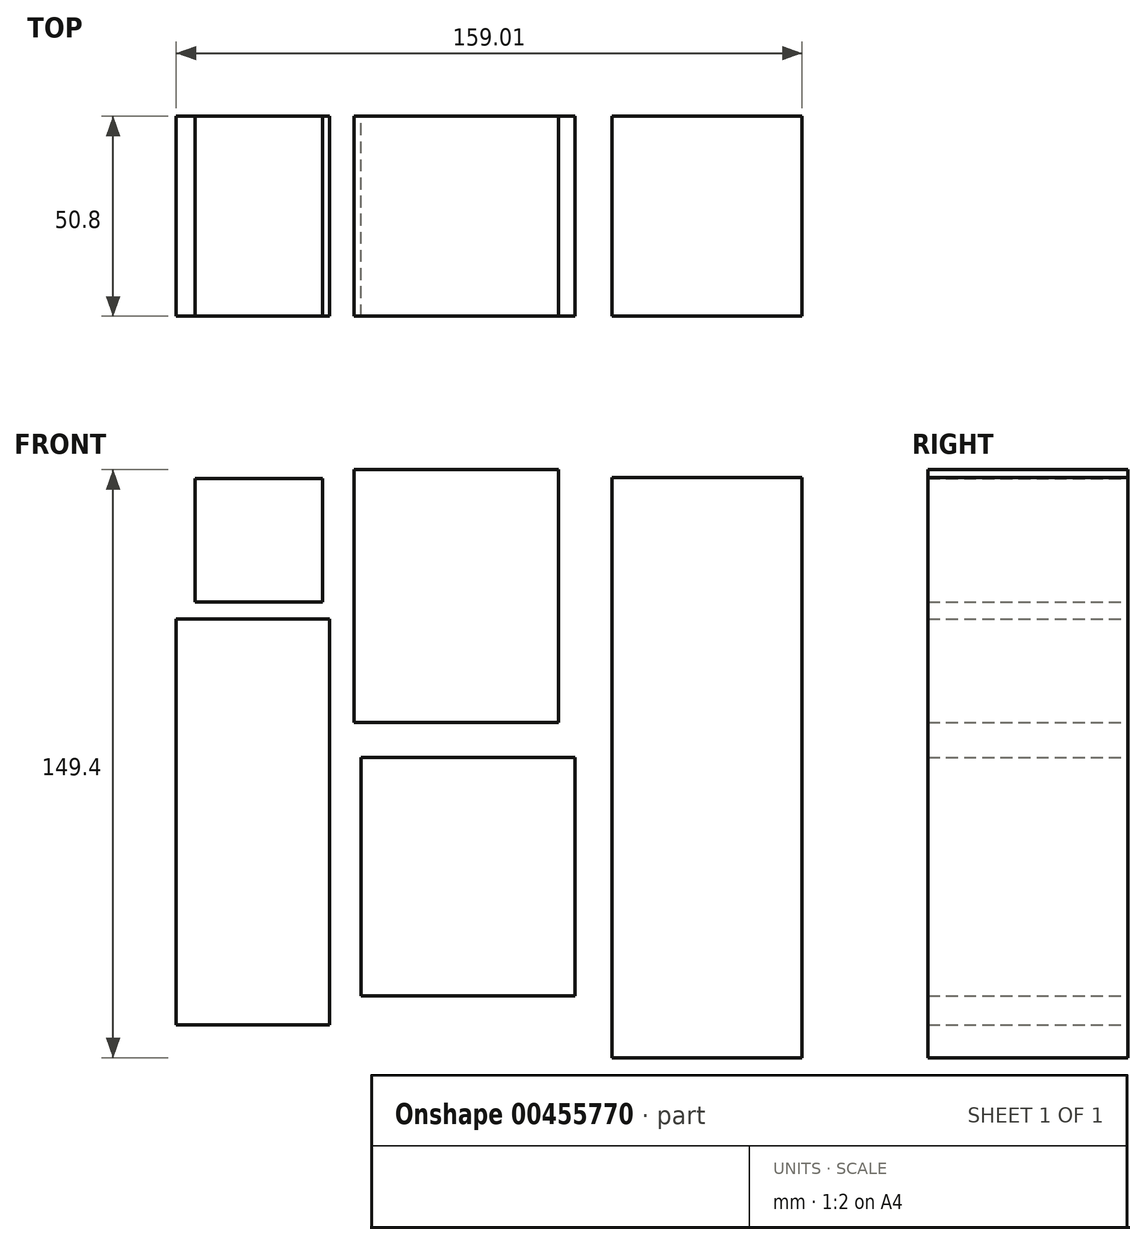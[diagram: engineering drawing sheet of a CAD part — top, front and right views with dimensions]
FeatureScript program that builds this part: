
annotation { "Feature Type Name" : "Feature", "Feature Type Description" : "" }
export const myFeature = defineFeature(function(context is Context, id is Id, definition is map)
    precondition{}
    {
        {
            var Q0;
            Q0=qCreatedBy(makeId("Front.planeOp"),FACE);
            var sketch = newSketch(context, id + "F0", { "sketchPlane" : qUnion([Q0])});
            skLineSegment(sketch, "E0.bottom", {"start": v(-22.75, 73.18) * mm, "end": v(29.07, 73.18) * mm});
            skLineSegment(sketch, "E0.top", {"start": v(-22.75, 8.97) * mm, "end": v(29.07, 8.97) * mm});
            skLineSegment(sketch, "E0.left", {"start": v(-22.75, 73.18) * mm, "end": v(-22.75, 8.97) * mm});
            skLineSegment(sketch, "E0.right", {"start": v(29.07, 73.18) * mm, "end": v(29.07, 8.97) * mm});
            skLineSegment(sketch, "E1.bottom", {"start": v(-29.07, 35.27) * mm, "end": v(-68, 35.27) * mm});
            skLineSegment(sketch, "E1.top", {"start": v(-29.07, -67.88) * mm, "end": v(-68, -67.88) * mm});
            skLineSegment(sketch, "E1.left", {"start": v(-29.07, 35.27) * mm, "end": v(-29.07, -67.88) * mm});
            skLineSegment(sketch, "E1.right", {"start": v(-68, 35.27) * mm, "end": v(-68, -67.88) * mm});
            skLineSegment(sketch, "E2.bottom", {"start": v(-20.98, 0) * mm, "end": v(33.37, 0) * mm});
            skLineSegment(sketch, "E2.top", {"start": v(-20.98, -60.54) * mm, "end": v(33.37, -60.54) * mm});
            skLineSegment(sketch, "E2.left", {"start": v(-20.98, 0) * mm, "end": v(-20.98, -60.54) * mm});
            skLineSegment(sketch, "E2.right", {"start": v(33.37, 0) * mm, "end": v(33.37, -60.54) * mm});
            skLineSegment(sketch, "E3.bottom", {"start": v(42.72, 71.16) * mm, "end": v(91, 71.16) * mm});
            skLineSegment(sketch, "E3.top", {"start": v(42.72, -76.22) * mm, "end": v(91, -76.22) * mm});
            skLineSegment(sketch, "E3.left", {"start": v(42.72, 71.16) * mm, "end": v(42.72, -76.22) * mm});
            skLineSegment(sketch, "E3.right", {"start": v(91, 71.16) * mm, "end": v(91, -76.22) * mm});
            skLineSegment(sketch, "E4.bottom", {"start": v(-30.84, 39.56) * mm, "end": v(-63.2, 39.56) * mm});
            skLineSegment(sketch, "E4.top", {"start": v(-30.84, 70.9) * mm, "end": v(-63.2, 70.9) * mm});
            skLineSegment(sketch, "E4.left", {"start": v(-30.84, 39.56) * mm, "end": v(-30.84, 70.9) * mm});
            skLineSegment(sketch, "E4.right", {"start": v(-63.2, 39.56) * mm, "end": v(-63.2, 70.9) * mm});
            skSolve(sketch);
        }
        {
            var Q0;
            Q0 = qSketchRegion(id + "F0", true);
            var Q1;
            Q1=makeQuery(id+"F0.imprint","IMPRINT",FACE,{"disambiguationData":[TD([[makeQuery(id+"F0.imprint","IMPRINT",EDGE,{"derivedFrom":sQuery(id+"F0.wireOp",EDGE,"E4.bottom")}),-1.0]])]});
            extrude(context, id + "F1", {"entities" : qUnion([Q0, Q1]), "depth" : 50.8 * mm});
        }
    });
